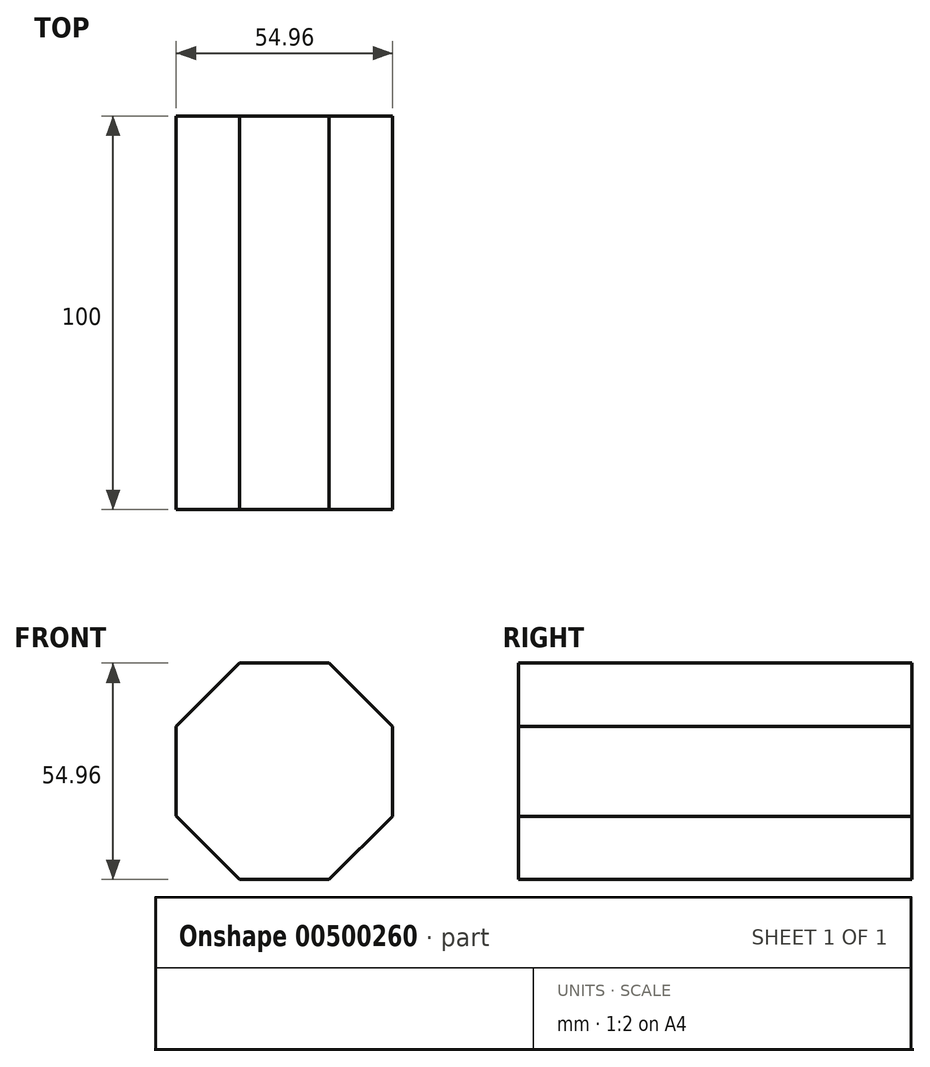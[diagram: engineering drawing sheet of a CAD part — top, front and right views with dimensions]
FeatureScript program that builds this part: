
annotation { "Feature Type Name" : "Feature", "Feature Type Description" : "" }
export const myFeature = defineFeature(function(context is Context, id is Id, definition is map)
    precondition{}
    {
        {
            var Q0;
            Q0=qCreatedBy(makeId("Front.planeOp"),FACE);
            var sketch = newSketch(context, id + "F0", { "sketchPlane" : qUnion([Q0])});
            skCircle(sketch, "E0.cCircle", {"center": v(0, 0) * mm, "radius": 29.74 * mm, "construction": true});
            skLineSegment(sketch, "E0.0", {"start": v(11.36, -27.48) * mm, "end": v(-11.4, -27.47) * mm});
            skLineSegment(sketch, "E0.1", {"start": v(-11.4, -27.47) * mm, "end": v(-27.48, -11.36) * mm});
            skLineSegment(sketch, "E0.2", {"start": v(-27.48, -11.36) * mm, "end": v(-27.47, 11.4) * mm});
            skLineSegment(sketch, "E0.3", {"start": v(-27.47, 11.4) * mm, "end": v(-11.36, 27.48) * mm});
            skLineSegment(sketch, "E0.4", {"start": v(-11.36, 27.48) * mm, "end": v(11.4, 27.47) * mm});
            skLineSegment(sketch, "E0.5", {"start": v(11.4, 27.47) * mm, "end": v(27.48, 11.36) * mm});
            skLineSegment(sketch, "E0.6", {"start": v(27.48, 11.36) * mm, "end": v(27.47, -11.4) * mm});
            skLineSegment(sketch, "E0.7", {"start": v(27.47, -11.4) * mm, "end": v(11.36, -27.48) * mm});
            skSolve(sketch);
        }
        {
            var Q0;
            Q0=makeQuery(id+"F0.imprint","IMPRINT",FACE,{"disambiguationData":[TD([[makeQuery(id+"F0.imprint","IMPRINT",EDGE,{"derivedFrom":sQuery(id+"F0.wireOp",EDGE,"E0.0")}),-1.0]])]});
            extrude(context, id + "F1", {"entities" : qUnion([Q0]), "depth" : 100 * mm});
        }
    });
